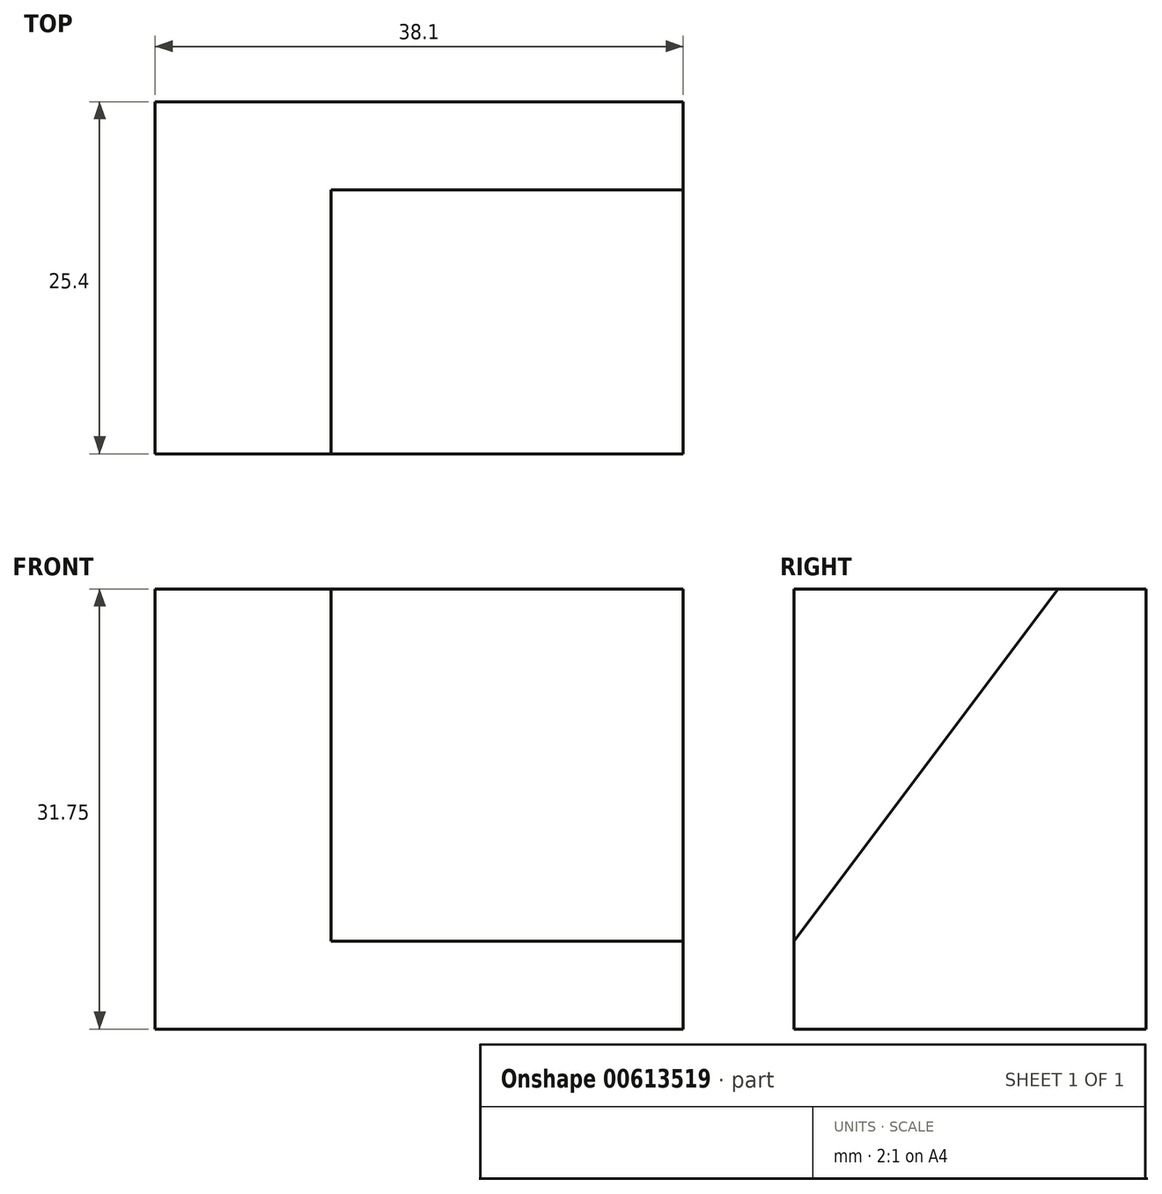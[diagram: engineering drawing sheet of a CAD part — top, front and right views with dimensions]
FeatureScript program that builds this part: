
annotation { "Feature Type Name" : "Feature", "Feature Type Description" : "" }
export const myFeature = defineFeature(function(context is Context, id is Id, definition is map)
    precondition{}
    {
        {
            var Q0;
            Q0=qCreatedBy(makeId("Front.planeOp"),FACE);
            var sketch = newSketch(context, id + "F0", { "sketchPlane" : qUnion([Q0])});
            skLineSegment(sketch, "E0.bottom", {"start": v(0, 0) * mm, "end": v(38.1, 0) * mm});
            skLineSegment(sketch, "E0.top", {"start": v(0, 31.75) * mm, "end": v(38.1, 31.75) * mm});
            skLineSegment(sketch, "E0.left", {"start": v(0, 0) * mm, "end": v(0, 31.75) * mm});
            skLineSegment(sketch, "E0.right", {"start": v(38.1, 0) * mm, "end": v(38.1, 31.75) * mm});
            skSolve(sketch);
        }
        {
            var Q0;
            Q0 = qSketchRegion(id + "F0", true);
            extrude(context, id + "F1", {"entities" : qUnion([Q0]), "depth" : 25.4 * mm, "offsetDistance" : 25.4 * mm});
        }
        {
            var Q0;
            Q0=makeQuery(id+"F1.opExtrude","SWEPT_FACE",FACE,{"disambiguationData":[OSD([sQuery(id+"F0.wireOp",EDGE,"E0.right")])]});
            var sketch = newSketch(context, id + "F2", { "sketchPlane" : qUnion([Q0])});
            skLineSegment(sketch, "E1", {"start": v(0, 31.75) * mm, "end": v(-6.35, 31.75) * mm});
            skLineSegment(sketch, "E2", {"start": v(-25.4, 0) * mm, "end": v(-25.4, 6.35) * mm});
            skLineSegment(sketch, "E3", {"start": v(-25.4, 6.35) * mm, "end": v(-6.35, 31.75) * mm});
            skSolve(sketch);
        }
        {
            var Q0;
            Q0 = qSketchRegion(id + "F2", true);
            var Q1;
            {var subQ0=sQuery(id+"F2.wireOp",EDGE,"E3");Q1=makeQuery(id+"F2.imprint","IMPRINT",FACE,{"disambiguationData":[TD([[makeQuery(id+"F2.imprint","IMPRINT",EDGE,{"derivedFrom":subQ0}),1.0]])]});}
            extrude(context, id + "F3", {"entities" : qUnion([Q0, Q1]), "operationType" : NewBodyOperationType.REMOVE, "oppositeDirection" : true, "depth" : 25.4 * mm, "offsetDistance" : 25.4 * mm});
        }
    });
